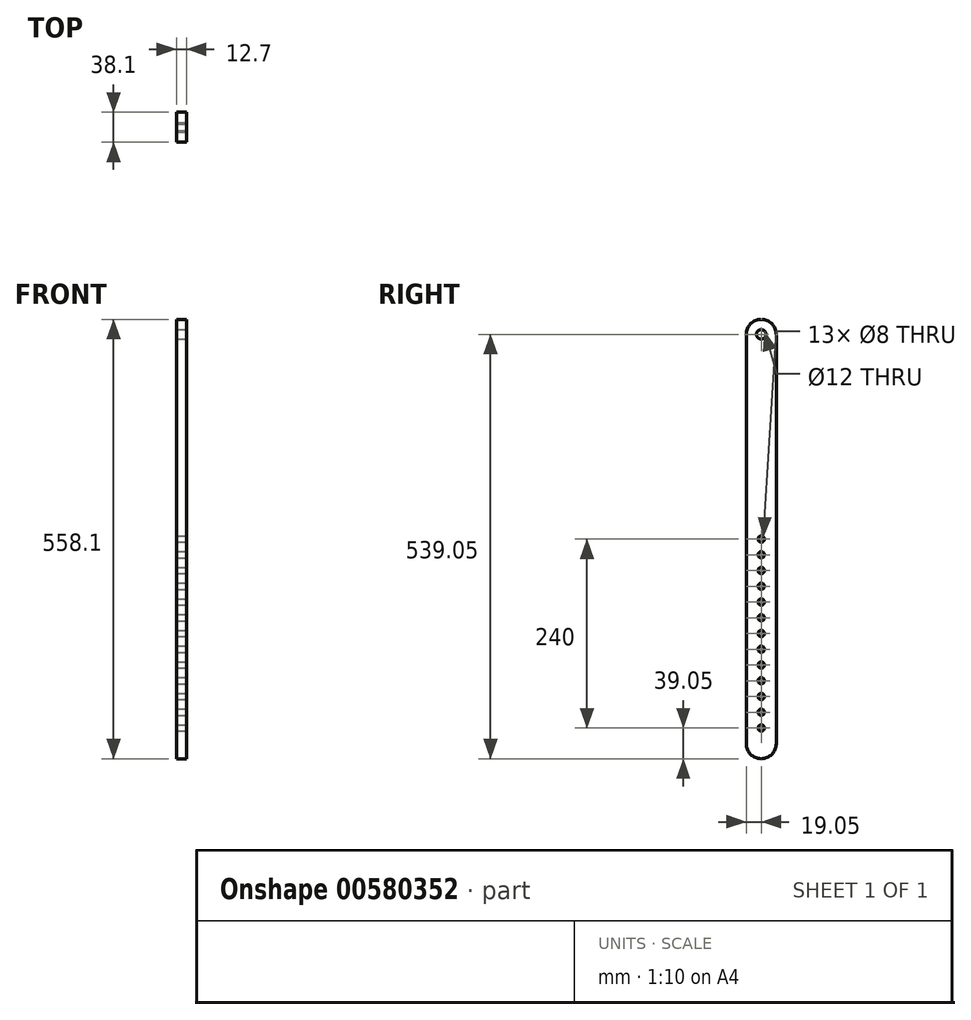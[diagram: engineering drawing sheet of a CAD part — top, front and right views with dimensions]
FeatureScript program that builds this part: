
annotation { "Feature Type Name" : "Feature", "Feature Type Description" : "" }
export const myFeature = defineFeature(function(context is Context, id is Id, definition is map)
    precondition{}
    {
        {
            var Q0;
            Q0=qCreatedBy(makeId("Right.planeOp"),FACE);
            var sketch = newSketch(context, id + "F0", { "sketchPlane" : qUnion([Q0])});
            skLineSegment(sketch, "E0", {"start": v(-19.05, 260) * mm, "end": v(-19.05, -260) * mm});
            skLineSegment(sketch, "E1", {"start": v(0, 54.22) * mm, "end": v(0, -50.31) * mm, "construction": true});
            skLineSegment(sketch, "E2.MirrorCS", {"start": v(19.05, 260) * mm, "end": v(19.05, -260) * mm});
            skArc(sketch, "E3", {"start": v(19.05, 260) * mm, "mid": v(0, 279.05) * mm, "end": v(-19.05, 260) * mm});
            skArc(sketch, "E4", {"start": v(-19.05, -260) * mm, "mid": v(0, -279.05) * mm, "end": v(19.05, -260) * mm});
            skLineSegment(sketch, "E5", {"start": v(-19.05, 0) * mm, "end": v(19.05, 0) * mm, "construction": true});
            skCircle(sketch, "E6", {"center": v(0, 260) * mm, "radius": 6 * mm});
            skCircle(sketch, "E7", {"center": v(0, 0) * mm, "radius": 4 * mm});
            skCircle(sketch, "E8.0.1.0", {"center": v(0, -20) * mm, "radius": 4 * mm});
            skCircle(sketch, "E8.0.2.0", {"center": v(0, -40) * mm, "radius": 4 * mm});
            skCircle(sketch, "E8.0.3.0", {"center": v(0, -60) * mm, "radius": 4 * mm});
            skCircle(sketch, "E8.0.4.0", {"center": v(0, -80) * mm, "radius": 4 * mm});
            skCircle(sketch, "E8.0.5.0", {"center": v(0, -100) * mm, "radius": 4 * mm});
            skCircle(sketch, "E8.0.6.0", {"center": v(0, -120) * mm, "radius": 4 * mm});
            skCircle(sketch, "E8.0.7.0", {"center": v(0, -140) * mm, "radius": 4 * mm});
            skCircle(sketch, "E8.0.8.0", {"center": v(0, -160) * mm, "radius": 4 * mm});
            skCircle(sketch, "E8.0.9.0", {"center": v(0, -180) * mm, "radius": 4 * mm});
            skCircle(sketch, "E8.0.10.0", {"center": v(0, -200) * mm, "radius": 4 * mm});
            skCircle(sketch, "E8.0.11.0", {"center": v(0, -220) * mm, "radius": 4 * mm});
            skCircle(sketch, "E8.0.12.0", {"center": v(0, -240) * mm, "radius": 4 * mm});
            skLineSegment(sketch, "E8.direction1", {"start": v(0, 0) * mm, "end": v(25, 0) * mm, "construction": true});
            skLineSegment(sketch, "E8.direction2", {"start": v(0, 0) * mm, "end": v(0, -20) * mm, "construction": true});
            skSolve(sketch);
        }
        {
            var Q0;
            Q0 = qSketchRegion(id + "F0", true);
            extrude(context, id + "F1", {"entities" : qUnion([Q0]), "oppositeDirection" : true, "depth" : 12.7 * mm, "offsetDistance" : 25 * mm});
        }
    });
